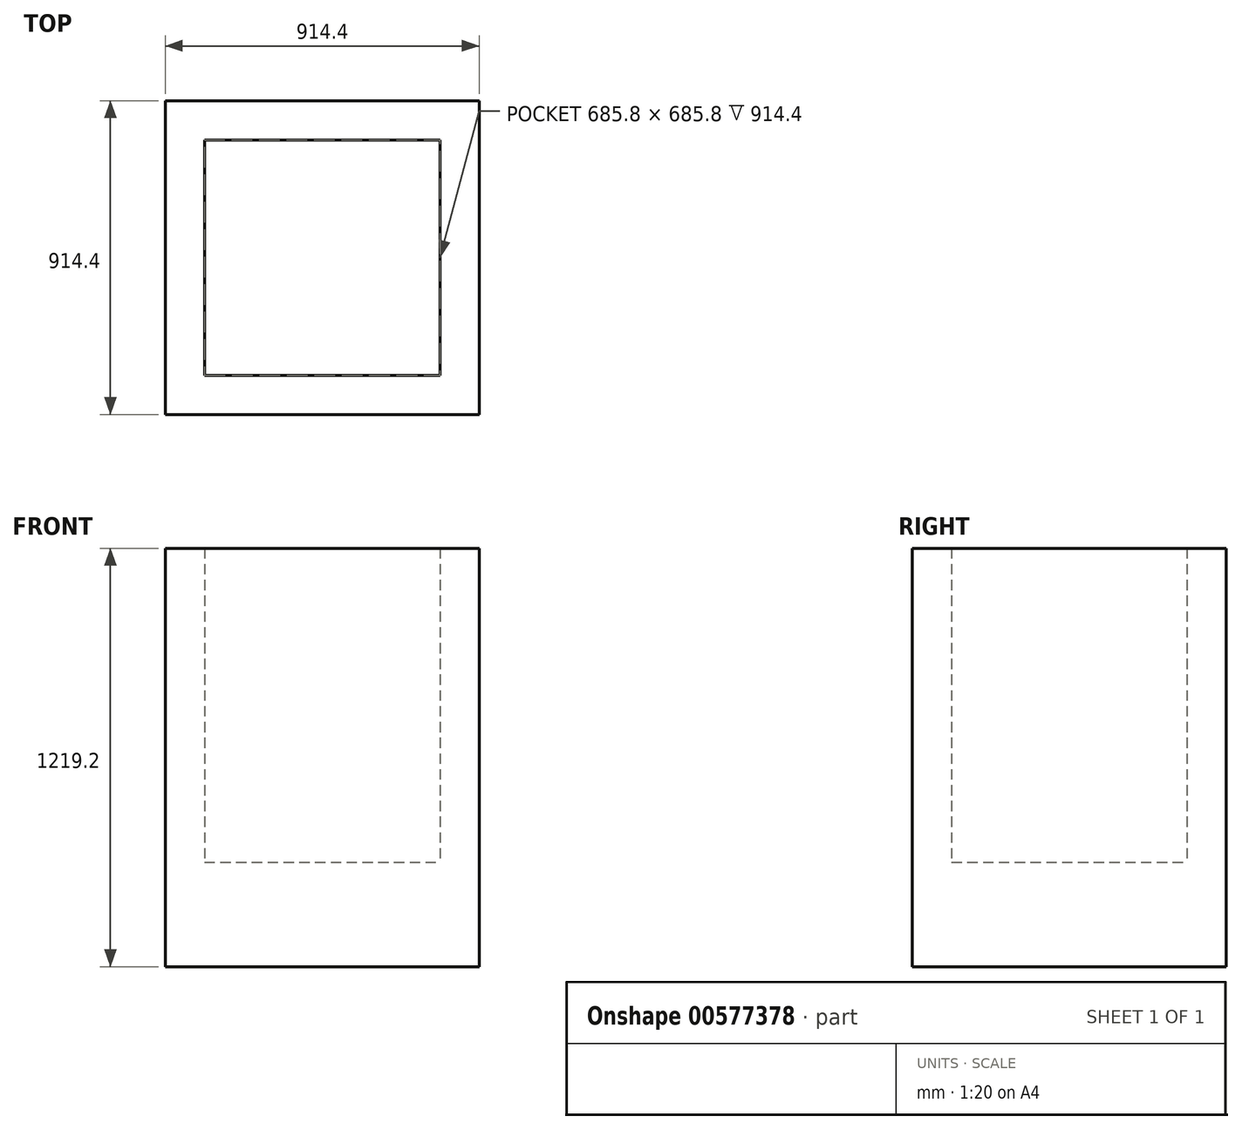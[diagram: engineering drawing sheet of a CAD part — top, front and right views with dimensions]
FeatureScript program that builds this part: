
annotation { "Feature Type Name" : "Feature", "Feature Type Description" : "" }
export const myFeature = defineFeature(function(context is Context, id is Id, definition is map)
    precondition{}
    {
        {
            var Q0;
            Q0=qCreatedBy(makeId("Top.planeOp"),FACE);
            var sketch = newSketch(context, id + "F0", { "sketchPlane" : qUnion([Q0])});
            skLineSegment(sketch, "E0.bottom", {"start": v(-465.86, 525.04) * mm, "end": v(448.54, 525.04) * mm});
            skLineSegment(sketch, "E0.top", {"start": v(-465.86, -389.36) * mm, "end": v(448.54, -389.36) * mm});
            skLineSegment(sketch, "E0.left", {"start": v(-465.86, 525.04) * mm, "end": v(-465.86, -389.36) * mm});
            skLineSegment(sketch, "E0.right", {"start": v(448.54, 525.04) * mm, "end": v(448.54, -389.36) * mm});
            skSolve(sketch);
        }
        {
            var Q0;
            Q0=makeQuery(id+"F0.imprint","IMPRINT",FACE,{"disambiguationData":[TD([[makeQuery(id+"F0.imprint","IMPRINT",EDGE,{"derivedFrom":sQuery(id+"F0.wireOp",EDGE,"E0.bottom")}),-1.0]])]});
            extrude(context, id + "F1", {"entities" : qUnion([Q0]), "depth" : 304.8 * mm, "offsetDistance" : 25.4 * mm});
        }
        {
            var Q0;
            Q0=makeQuery(id+"F1.opExtrude","CAP_FACE",FACE,{"disambiguationData":[OSD([sQuery(id+"F0.wireOp",EDGE,"E0.bottom"),sQuery(id+"F0.wireOp",EDGE,"E0.top"),sQuery(id+"F0.wireOp",EDGE,"E0.left"),sQuery(id+"F0.wireOp",EDGE,"E0.right")])],"isStart":false});
            var sketch = newSketch(context, id + "F2", { "sketchPlane" : qUnion([Q0])});
            skLineSegment(sketch, "E1", {"start": v(-351.56, 410.74) * mm, "end": v(334.24, 410.74) * mm});
            skLineSegment(sketch, "E2", {"start": v(334.24, 410.74) * mm, "end": v(334.24, -275.06) * mm});
            skLineSegment(sketch, "E3", {"start": v(334.24, -275.06) * mm, "end": v(-351.56, -275.06) * mm});
            skLineSegment(sketch, "E4", {"start": v(-351.56, -275.06) * mm, "end": v(-351.56, 410.74) * mm});
            skPoint(sketch, "E5.orphan", {"position": v(-237.26, 296.44) * mm});
            skPoint(sketch, "E6.orphan", {"position": v(-8.66, 67.84) * mm});
            skPoint(sketch, "E7.start.orphan", {"position": v(-465.86, 525.04) * mm});
            skPoint(sketch, "E8.trimOffspring.end.orphan", {"position": v(448.54, -389.36) * mm});
            skSolve(sketch);
        }
        {
            var Q0;
            Q0=makeQuery(id+"F2.imprint","IMPRINT",FACE,{"disambiguationData":[TD([[makeQuery(id+"F2.imprint","IMPRINT",EDGE,{"derivedFrom":sQuery(id+"F2.wireOp",EDGE,"E1")}),1.0]])]});
            extrude(context, id + "F3", {"entities" : qUnion([Q0]), "operationType" : NewBodyOperationType.ADD, "depth" : 914.4 * mm, "offsetDistance" : 25.4 * mm});
        }
    });
